# Revit family: STL23931_30_40_50
name_source: partatom
category: Luminárias
units: mm (PartAtom-declared; Revit-internal decimal feet)

## family parameters
Compartilhado = Não
Corte com vazios quando carregada = Não
Cota do conector redondo = Utilizar diâmetro
Fonte luminosa = Sim
Hospedeiro = Forro
Manter orientação da anotação = Não
Número OmniClass = 23.80.70.11
Ponto de cálculo do ambiente = Não
Sempre na vertical = Sim
Tipo de parte = Normal
Título OmniClass = Luminaries for Internal Lighting

## types (3) — shared parameters
Altura = 0.04 m
Comprimento = 0.6 m
Dimerização = Não dimerizável
Estrutura = Al - Branco
Fabricante = Stella
Filtro de cor = 16777215
Grau de proteção (IP) = IP20
IRC (Índice de reprodução de cores) = >80
Largura = 0.07 m
Modelo = Plane
Potência = 16 W
Tensão Elétrica = 100V-240V
Troca de temperatura da cor de lâmpada com esmaecimento = <Nenhum>
URL = https://stella.com.br
Ângulo de Abertura = 140º
Ângulo de inclinação = 90.00°
zero-valued in all types: Elevação padrão

## per-type parameters (varying)
| type | Arquivo de rede fotométrica | Fluxo Luminoso | Luminoso | Referência | Temperatura da cor (K) |
| STL23931/30 - BRANCO - 3000K - 1800lm - 140º | STELLA - STL23931-30 - LUMINARIA DE SOBREPOR PLANE 60CM.ies | 1800 lm | Luminoso - 3000K | STL23931/30 - BRANCO | 3000 K |
| STL23931/40 - BRANCO - 4000K - 1900lm - 140° | STELLA - STL23931-40 - LUMINARIA DE SOBREPOR PLANE 60CM.ies | 1900 lm | Luminoso - 4000K | STL23931/40 - BRANCO | 4000 K |
| STL23931/50 - BRANCO - 5000K - 2000lm - 140° | STELLA - STL23931-50 - LUMINARIA DE SOBREPOR PLANE 60CM.ies | 2000 lm | Luminoso - 5000K | STL23931/50 - BRANCO | 5000 K |
